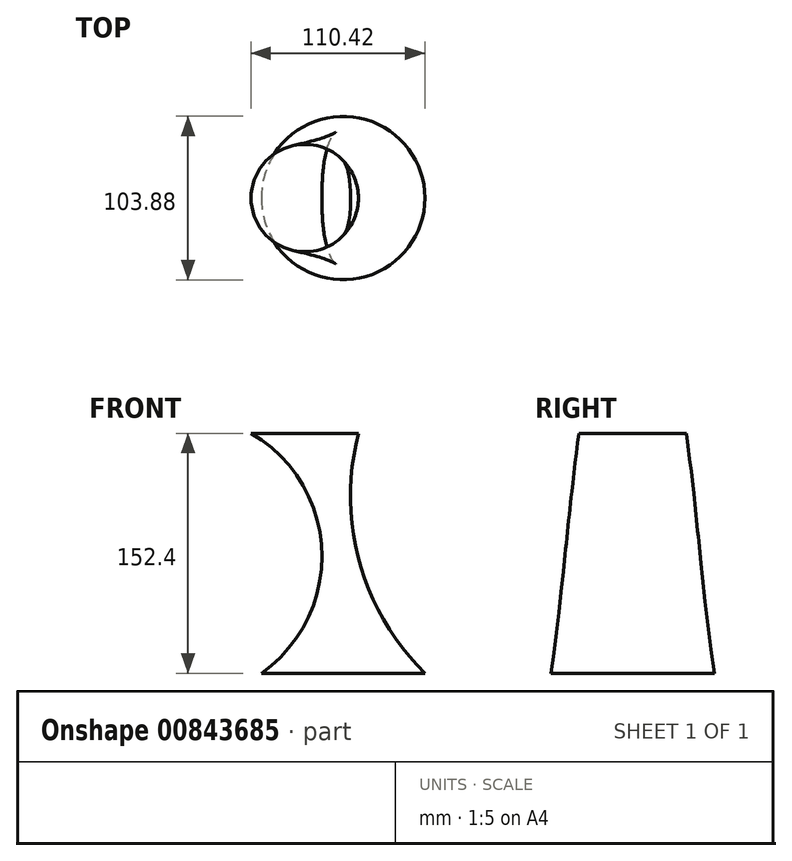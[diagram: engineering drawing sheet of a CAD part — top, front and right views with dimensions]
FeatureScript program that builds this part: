
annotation { "Feature Type Name" : "Feature", "Feature Type Description" : "" }
export const myFeature = defineFeature(function(context is Context, id is Id, definition is map)
    precondition{}
    {
        {
            var Q0;
            Q0=qCreatedBy(makeId("Top.planeOp"),FACE);
            var sketch = newSketch(context, id + "F0", { "sketchPlane" : qUnion([Q0])});
            skCircle(sketch, "E0", {"center": v(0, 0) * mm, "radius": 51.94 * mm});
            skSolve(sketch);
        }
        {
            var Q0;
            Q0=qCreatedBy(makeId("Front.planeOp"),FACE);
            var sketch = newSketch(context, id + "F1", { "sketchPlane" : qUnion([Q0])});
            skArc(sketch, "E1", {"start": v(9.74, 152.4) * mm, "mid": v(10.47, 70.56) * mm, "end": v(51.94, 0) * mm});
            skArc(sketch, "E2", {"start": v(-51.94, 0) * mm, "mid": v(-13.55, 77.99) * mm, "end": v(-58.48, 152.4) * mm});
            skSolve(sketch);
        }
        {
            var Q0;
            Q0=qCreatedBy(makeId("Top.planeOp"),FACE);
            cPlane(context, id + "F2", {"entities" : qUnion([Q0]), "cplaneType" : CPlaneType.OFFSET, "offset" : 76.2 * mm, "width" : 152.4 * mm, "height" : 152.4 * mm});
        }
        {
            var Q0;
            Q0=qCreatedBy(id+"F2.planeOp",FACE);
            cPlane(context, id + "F3", {"entities" : qUnion([Q0]), "cplaneType" : CPlaneType.OFFSET, "offset" : 76.2 * mm, "width" : 152.4 * mm, "height" : 152.4 * mm});
        }
        {
            var Q0;
            Q0=qCreatedBy(id+"F3.planeOp",FACE);
            var sketch = newSketch(context, id + "F4", { "sketchPlane" : qUnion([Q0])});
            skCircle(sketch, "E3", {"center": v(-24.37, 0) * mm, "radius": 34.1 * mm});
            skSolve(sketch);
        }
        {
            var Q0;
            Q0=sQuery(id+"F1.wireOp",EDGE,"E1");
            var Q1;
            Q1=sQuery(id+"F1.wireOp",EDGE,"E2");
            var Q2;
            Q2=makeQuery(id+"F0.imprint","IMPRINT",FACE,{"disambiguationData":[TD([[makeQuery(id+"F0.imprint","IMPRINT",EDGE,{"derivedFrom":sQuery(id+"F0.wireOp",EDGE,"E0")}),1.0]])]});
            var Q3;
            Q3=makeQuery(id+"F4.imprint","IMPRINT",FACE,{"disambiguationData":[TD([[makeQuery(id+"F4.imprint","IMPRINT",EDGE,{"derivedFrom":sQuery(id+"F4.wireOp",EDGE,"E3")}),1.0]])]});
            var Q4;
            Q4=sQuery(id+"F0.wireOp",EDGE,"E0");
            var Q5;
            Q5=sQuery(id+"F4.wireOp",EDGE,"E3");
            var Q6;
            Q6=sQuery(id+"F1.wireOp",EDGE,"E2");
            var Q7;
            Q7=sQuery(id+"F1.wireOp",EDGE,"E1");
            loft(context, id + "F5", {"bodyType" : ToolBodyType.SURFACE, "spine" : qUnion([Q0, Q1]), "addGuides" : true, "sheetProfilesArray" : [{ "sheetProfileEntities" : qUnion([Q2]) }, { "sheetProfileEntities" : qUnion([Q3]) }], "wireProfilesArray" : [{ "wireProfileEntities" : qUnion([Q4]) }, { "wireProfileEntities" : qUnion([Q5]) }], "guidesArray" : [{ "guideEntities" : qUnion([Q6]), "guideDerivativeType" : LoftGuideDerivativeType.DEFAULT, "guideDerivativeMagnitude" : 1 }, { "guideEntities" : qUnion([Q7]), "guideDerivativeType" : LoftGuideDerivativeType.DEFAULT, "guideDerivativeMagnitude" : 1 }]});
        }
    });
